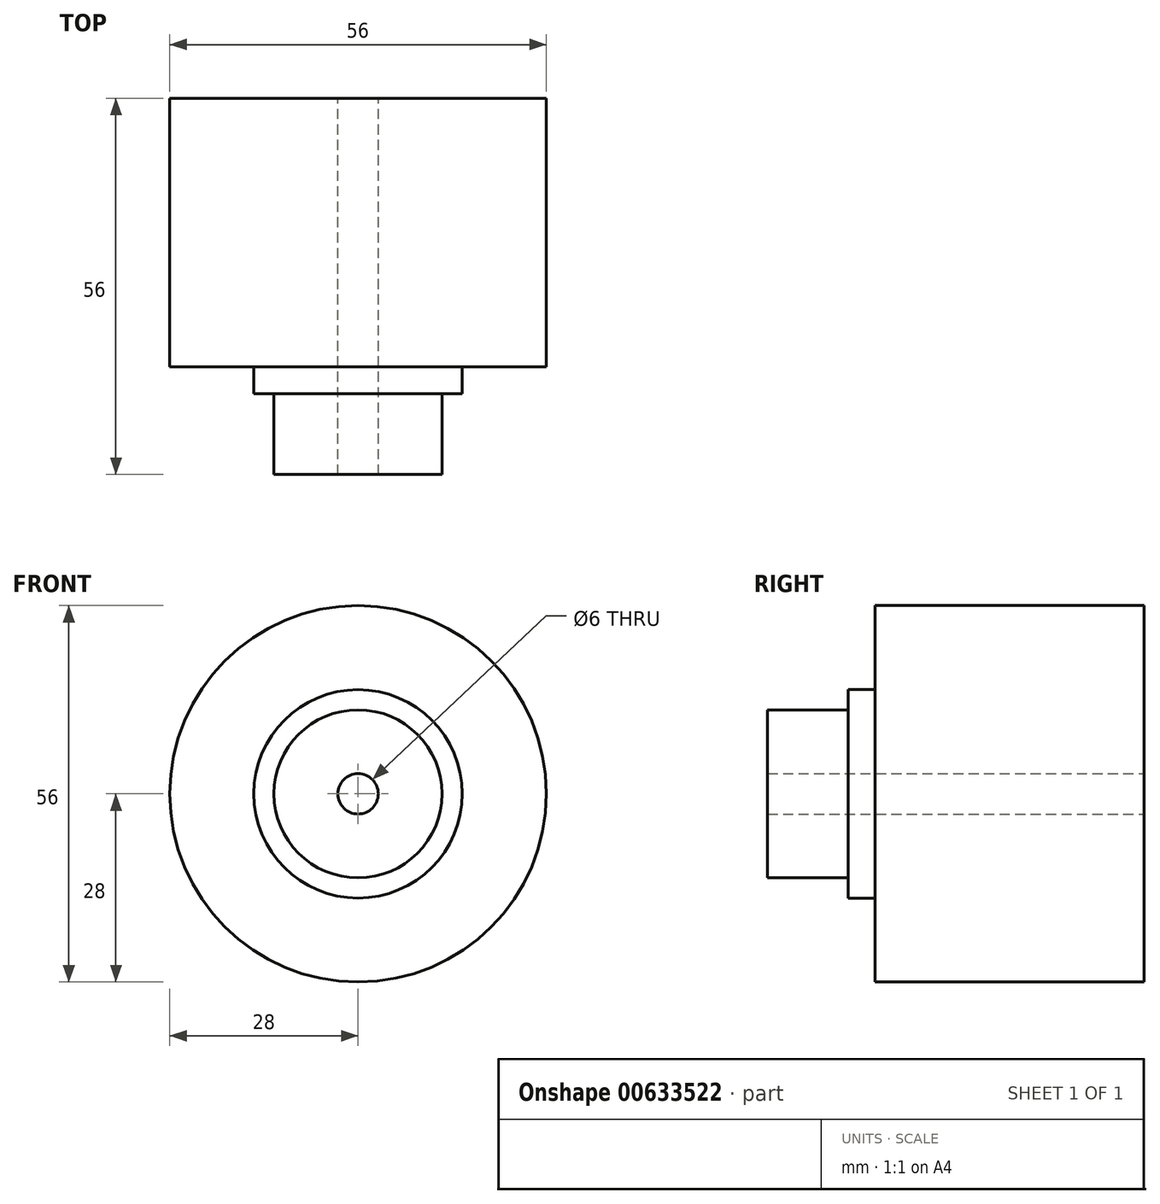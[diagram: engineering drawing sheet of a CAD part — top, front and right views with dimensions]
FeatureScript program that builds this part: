
annotation { "Feature Type Name" : "Feature", "Feature Type Description" : "" }
export const myFeature = defineFeature(function(context is Context, id is Id, definition is map)
    precondition{}
    {
        {
            var Q0;
            Q0=qCreatedBy(makeId("Front.planeOp"),FACE);
            var sketch = newSketch(context, id + "F0", { "sketchPlane" : qUnion([Q0])});
            skCircle(sketch, "E0", {"center": v(0, 0) * mm, "radius": 28 * mm});
            skCircle(sketch, "E1", {"center": v(0, 0) * mm, "radius": 3 * mm});
            skCircle(sketch, "E2", {"center": v(0, 0) * mm, "radius": 12.5 * mm});
            skCircle(sketch, "E3", {"center": v(0, 0) * mm, "radius": 15.5 * mm});
            skSolve(sketch);
        }
        {
            var Q0;
            Q0=makeQuery(id+"F0.imprint","IMPRINT",FACE,{"disambiguationData":[TD([[makeQuery(id+"F0.imprint","IMPRINT",EDGE,{"derivedFrom":sQuery(id+"F0.wireOp",EDGE,"E1")}),-1.0]])]});
            extrude(context, id + "F1", {"entities" : qUnion([Q0]), "depth" : 56 * mm, "offsetDistance" : 25 * mm});
        }
        {
            var Q0;
            Q0=makeQuery(id+"F0.imprint","IMPRINT",FACE,{"disambiguationData":[TD([[makeQuery(id+"F0.imprint","IMPRINT",EDGE,{"derivedFrom":sQuery(id+"F0.wireOp",EDGE,"E2")}),-1.0]])]});
            extrude(context, id + "F2", {"entities" : qUnion([Q0]), "operationType" : NewBodyOperationType.ADD, "depth" : 44 * mm, "offsetDistance" : 25 * mm});
        }
        {
            var Q0;
            Q0=makeQuery(id+"F0.imprint","IMPRINT",FACE,{"disambiguationData":[TD([[makeQuery(id+"F0.imprint","IMPRINT",EDGE,{"derivedFrom":sQuery(id+"F0.wireOp",EDGE,"E0")}),1.0]])]});
            extrude(context, id + "F3", {"entities" : qUnion([Q0]), "operationType" : NewBodyOperationType.ADD, "depth" : 40 * mm, "offsetDistance" : 25 * mm});
        }
    });
